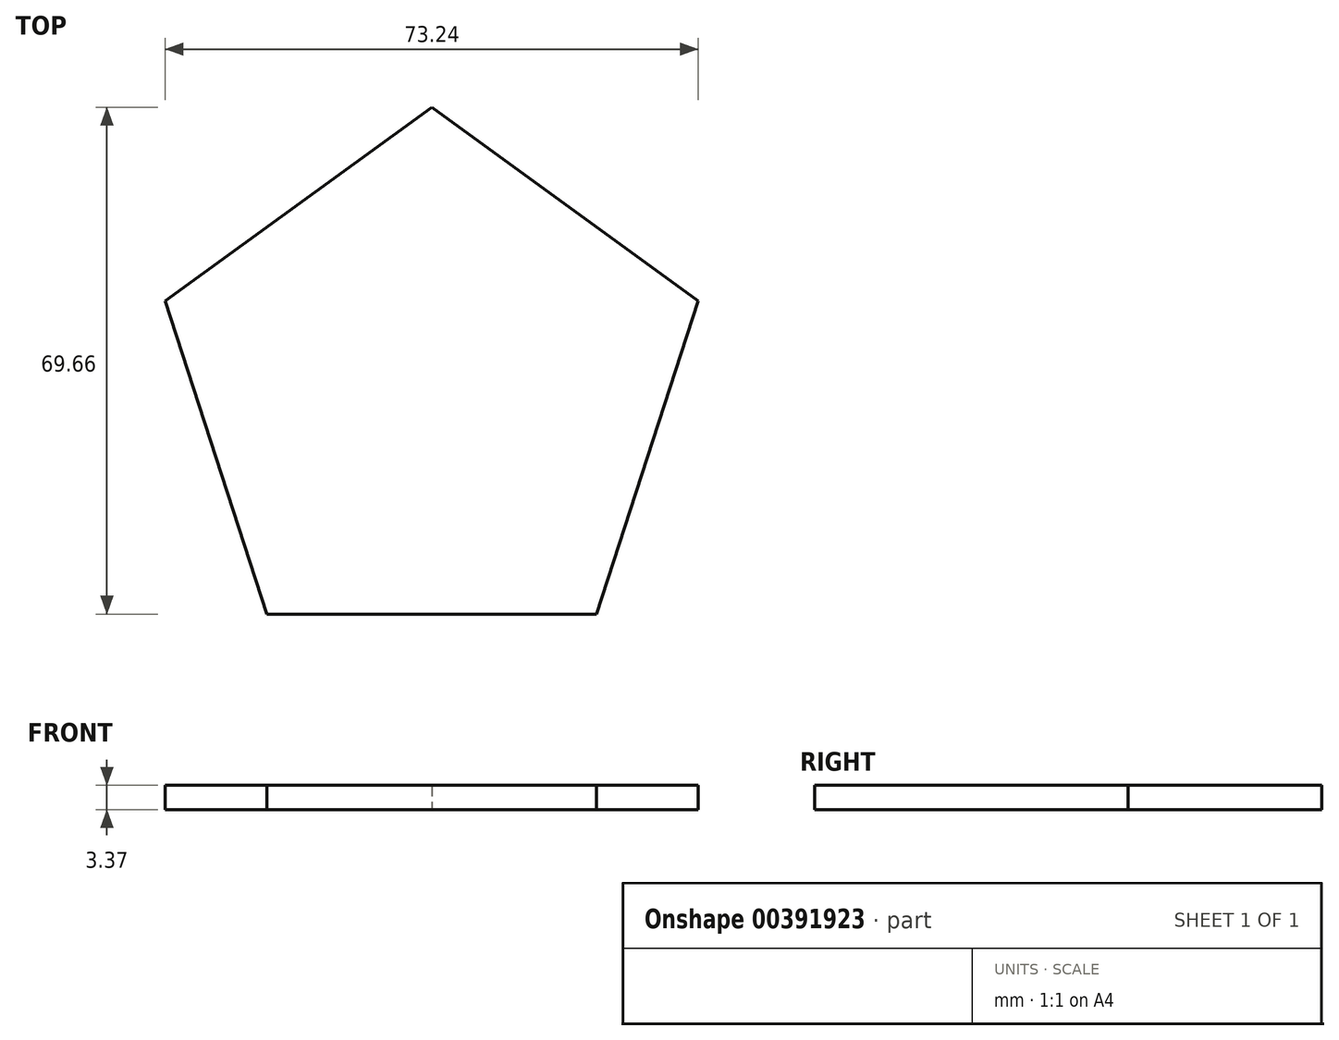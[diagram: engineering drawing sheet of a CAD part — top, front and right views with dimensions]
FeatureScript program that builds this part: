
annotation { "Feature Type Name" : "Feature", "Feature Type Description" : "" }
export const myFeature = defineFeature(function(context is Context, id is Id, definition is map)
    precondition{}
    {
        {
            var Q0;
            Q0=qCreatedBy(makeId("Top.planeOp"),FACE);
            var sketch = newSketch(context, id + "F0", { "sketchPlane" : qUnion([Q0])});
            skCircle(sketch, "E0.cCircle", {"center": v(0, 46.89) * mm, "radius": 31.15 * mm, "construction": true});
            skLineSegment(sketch, "E0.0", {"start": v(22.63, 15.73) * mm, "end": v(-22.63, 15.73) * mm});
            skLineSegment(sketch, "E0.1", {"start": v(-22.63, 15.73) * mm, "end": v(-36.62, 58.79) * mm});
            skLineSegment(sketch, "E0.2", {"start": v(-36.62, 58.79) * mm, "end": v(0, 85.4) * mm});
            skLineSegment(sketch, "E0.3", {"start": v(0, 85.4) * mm, "end": v(36.62, 58.79) * mm});
            skLineSegment(sketch, "E0.4", {"start": v(36.62, 58.79) * mm, "end": v(22.63, 15.73) * mm});
            skPoint(sketch, "E0.0.midPoint", {"position": v(0, 15.73) * mm});
            skSolve(sketch);
        }
        {
            var Q0;
            Q0 = qSketchRegion(id + "F0", true);
            extrude(context, id + "F1", {"entities" : qUnion([Q0]), "depth" : 3.37 * mm});
        }
    });
